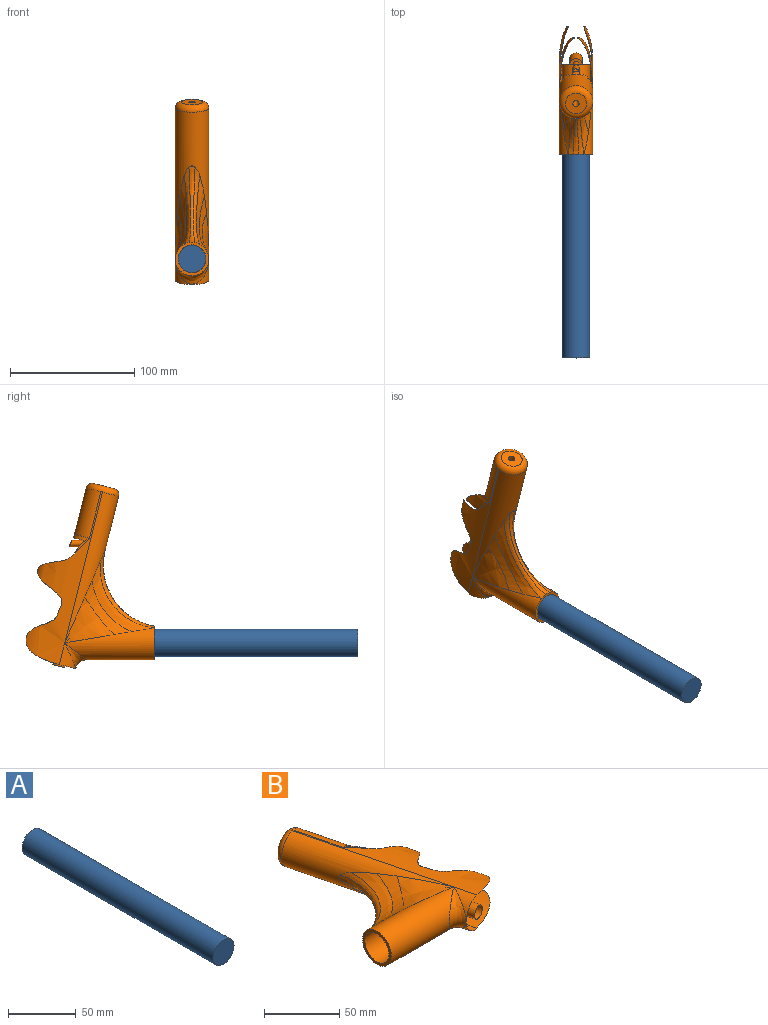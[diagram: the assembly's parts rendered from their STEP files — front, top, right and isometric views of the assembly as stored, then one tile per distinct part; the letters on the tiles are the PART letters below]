
ASSEMBLY  parts=2 mates=1
PART A: 3 faces, bbox 22x200x22 mm
  f0: cylinder r=11mm len=200mm, axis (0,1,0), area 13823mm2, adj f1,f2
  f1: plane 22x22mm, normal (0,-1,0), area 380.1mm2, adj f0
  f2: plane 22x22mm, normal (0,1,0), area 380.1mm2, adj f0
PART B: 30 faces, bbox 111x151x70.6 mm
  f0: cylinder r=2.5mm len=116.7mm, axis (-0.24,0.97,0), area 1846.6mm2, adj f2,f15,f27,f28,f29
  f1: revolved ~105.44x78.8mm, area 3338.7mm2, adj f11,f16,f17,f24,f26,f29
  f2: cylinder r=11.25mm len=72mm, axis (-1,0,0), area 5069.1mm2, adj f0,f3,f18,f24
  f3: plane 22.87x22mm, normal (-1,0,0), area 252.7mm2, adj f2,f23,f24,f25
  f4: bspline ~43.76x38.11mm, area 398.6mm2, adj f5,f10,f12,f19
  f5: bspline ~57.97x50.17mm, area 590.8mm2, adj f4,f6,f12,f19
  f6: bspline ~61.74x43.56mm, area 309.8mm2, adj f5,f7,f12,f18
  f7: bspline ~61.43x52.32mm, area 281.3mm2, adj f6,f8,f12,f18
  f8: bspline ~61.74x43.56mm, area 309.7mm2, adj f7,f9,f12,f18
  f9: bspline ~57.97x50.17mm, area 590.8mm2, adj f8,f12,f19,f22
  f10: bspline ~39.91x37.03mm, area 447mm2, adj f4,f12,f19
  f11: cylinder r=13.5mm len=27mm, axis (0.24,-0.97,0), area 287.2mm2, adj f1,f16,f17,f20
  f12: cylinder r=13.5mm len=124.55mm, axis (0.24,-0.97,0), area 3135.8mm2, adj f4,f5,f6,f7,f8,f9,f10,f14
  f13: cylinder r=13.5mm len=40.31mm, axis (0.24,-0.97,0), area 1542.1mm2, adj f14,f16,f17,f26
  f14: torus R=8.5mm, axis (0.24,-0.97,0), area 575.9mm2, adj f12,f13,f15,f16,f17
  f15: plane 17x16.5mm, normal (-0.24,0.97,0), area 207.3mm2, adj f0,f14
  f16: extruded ~147.26x68.83mm, area 2151.4mm2, adj f1,f11,f12,f13,f14,f26
  f17: extruded ~147.26x68.83mm, area 2143.1mm2, adj f1,f11,f12,f13,f14,f26
  f18: plane 27.02x27.02mm, normal (-1,0,0), area 174.9mm2, adj f2,f6,f7,f8,f19
  f19: cylinder r=13.5mm len=72mm, axis (-1,0,0), area 3532.3mm2, adj f4,f5,f9,f10,f18,f20,f21,f22
  f20: bspline ~27x20.32mm, area 107.1mm2, adj f11,f19
  f21: bspline ~43.48x40.44mm, area 447mm2, adj f12,f19,f22
  f22: bspline ~43.76x38.11mm, area 398.6mm2, adj f9,f12,f19,f21
  f23: cylinder r=2.5mm len=10.37mm, axis (-0.24,0.97,0), area 50.1mm2, adj f3,f25
  f24: cylinder r=5mm len=21.15mm, axis (0.24,-0.97,0), area 474.7mm2, adj f1,f2,f3,f25
  f25: plane 10x4.85mm, normal (0.24,-0.97,0), area 29.5mm2, adj f3,f23,f24
  f26: torus R=23.5mm, axis (0.24,-0.97,0), area 104.8mm2, adj f1,f13,f16,f17
  f27: plane 4.01x2.29mm, normal (1,0,0), area 2.9mm2, adj f0,f29
  f28: plane 4.01x2.29mm, normal (1,0,0), area 2.9mm2, adj f0,f29
  f29: cylinder r=2.5mm len=14.51mm, axis (-1,0,0), area 205.7mm2, adj f0,f1,f27,f28
PLACE A t=(-35.38,49.08,-45.74)mm fixed
PLACE B rot(axis=(0.58,0.58,0.58),120deg) t=(-35.38,13.08,-45.74)mm
MATE fastened B.f2 <-> A.f0  axis (0,-1,0) through (-35.38,49.08,-45.74)mm
